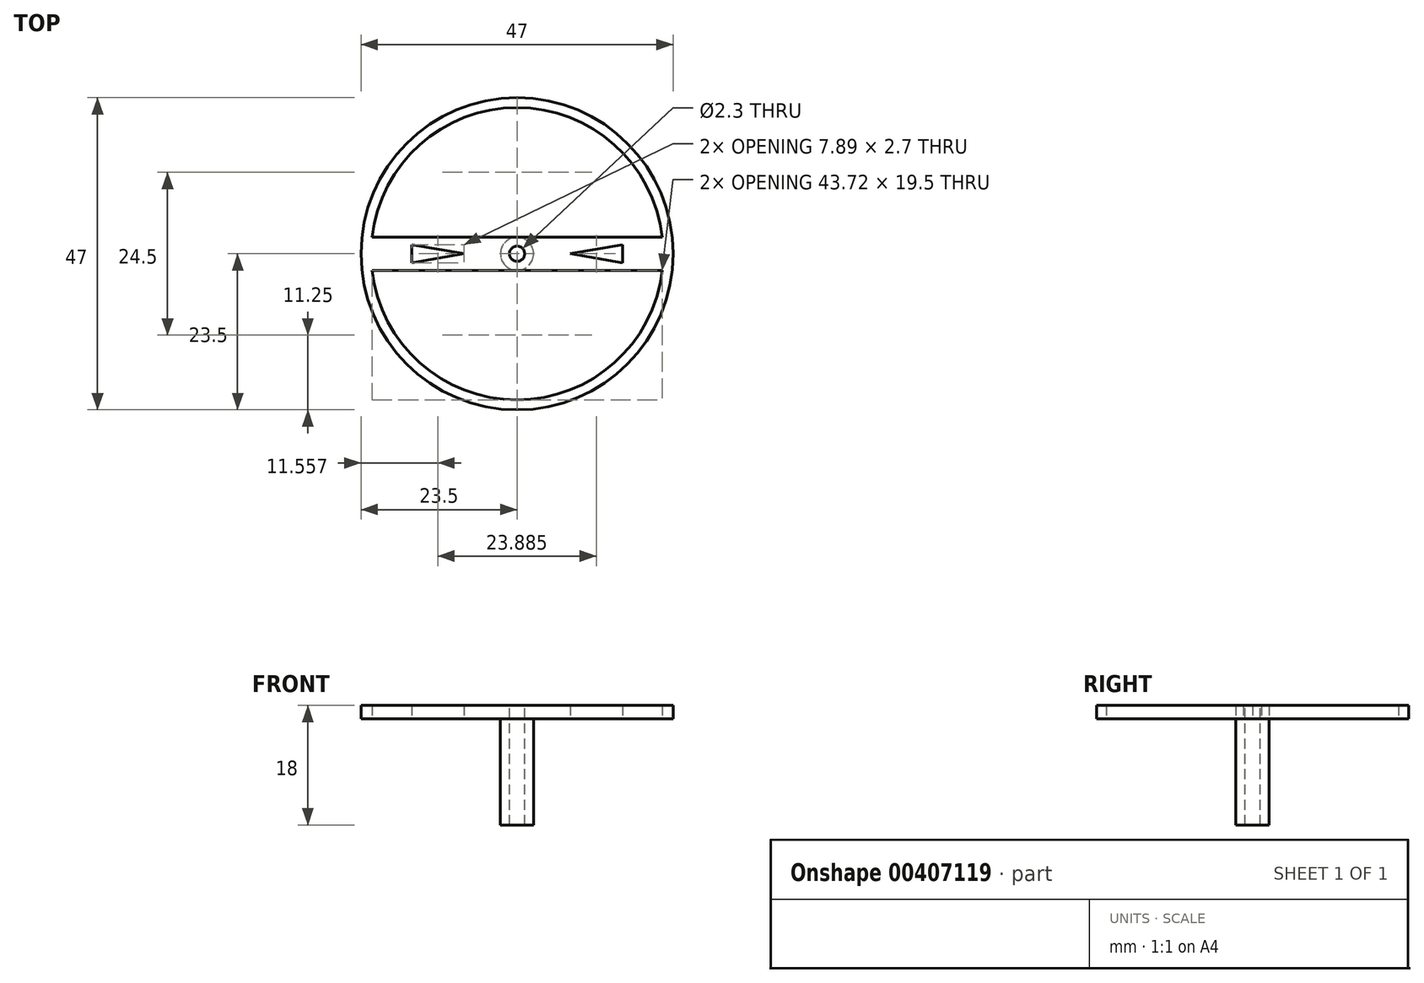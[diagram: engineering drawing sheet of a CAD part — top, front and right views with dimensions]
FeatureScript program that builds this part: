
annotation { "Feature Type Name" : "Feature", "Feature Type Description" : "" }
export const myFeature = defineFeature(function(context is Context, id is Id, definition is map)
    precondition{}
    {
        {
            var Q0;
            Q0=qCreatedBy(makeId("Top.planeOp"),FACE);
            var sketch = newSketch(context, id + "F0", { "sketchPlane" : qUnion([Q0])});
            skCircle(sketch, "E0", {"center": v(0, 0) * mm, "radius": 23.5 * mm});
            skCircle(sketch, "E1", {"center": v(0, 0) * mm, "radius": 22 * mm});
            skCircle(sketch, "E2", {"center": v(0, 0) * mm, "radius": 1.15 * mm});
            skCircle(sketch, "E3", {"center": v(0, 0) * mm, "radius": 2.5 * mm});
            skLineSegment(sketch, "E4", {"start": v(-21.86, 2.5) * mm, "end": v(21.86, 2.5) * mm});
            skLineSegment(sketch, "E5", {"start": v(-21.86, -2.5) * mm, "end": v(21.86, -2.5) * mm});
            skLineSegment(sketch, "E6", {"start": v(-15.89, 1.35) * mm, "end": v(-15.89, -1.35) * mm});
            skLineSegment(sketch, "E7", {"start": v(-15.89, -1.35) * mm, "end": v(-8, 0) * mm});
            skLineSegment(sketch, "E8", {"start": v(-8, 0) * mm, "end": v(-15.89, 1.35) * mm});
            skLineSegment(sketch, "E9.MirrorCS", {"start": v(15.89, -1.35) * mm, "end": v(8, 0) * mm});
            skLineSegment(sketch, "E10.MirrorCS", {"start": v(8, 0) * mm, "end": v(15.89, 1.35) * mm});
            skLineSegment(sketch, "E11.MirrorCS", {"start": v(15.89, 1.35) * mm, "end": v(15.89, -1.35) * mm});
            skSolve(sketch);
        }
        {
            var Q0;
            Q0=makeQuery(id+"F0.imprint","IMPRINT",FACE,{"disambiguationData":[TD([[makeQuery(id+"F0.imprint","IMPRINT",EDGE,{"derivedFrom":sQuery(id+"F0.wireOp",EDGE,"E2")}),-1.0]])]});
            extrude(context, id + "F1", {"entities" : qUnion([Q0]), "oppositeDirection" : true, "depth" : 16 * mm});
        }
        {
            var Q0;
            Q0=makeQuery(id+"F0.imprint","IMPRINT",FACE,{"disambiguationData":[TD([[makeQuery(id+"F0.imprint","IMPRINT",EDGE,{"derivedFrom":sQuery(id+"F0.wireOp",EDGE,"E2")}),-1.0]])]});
            var Q1;
            Q1=makeQuery(id+"F0.imprint","IMPRINT",FACE,{"disambiguationData":[TD([[makeQuery(id+"F0.imprint","IMPRINT",EDGE,{"derivedFrom":sQuery(id+"F0.wireOp",EDGE,"E9.MirrorCS")}),1.0]])]});
            var Q2;
            Q2=makeQuery(id+"F0.imprint","IMPRINT",FACE,{"disambiguationData":[TD([[makeQuery(id+"F0.imprint","IMPRINT",EDGE,{"derivedFrom":sQuery(id+"F0.wireOp",EDGE,"E6")}),-1.0]])]});
            var Q3;
            Q3=makeQuery(id+"F0.imprint","IMPRINT",FACE,{"disambiguationData":[TD([[makeQuery(id+"F0.imprint","IMPRINT",EDGE,{"derivedFrom":sQuery(id+"F0.wireOp",EDGE,"E0")}),1.0]])]});
            extrude(context, id + "F2", {"entities" : qUnion([Q0, Q1, Q2, Q3]), "operationType" : NewBodyOperationType.ADD, "depth" : 2 * mm});
        }
    });
